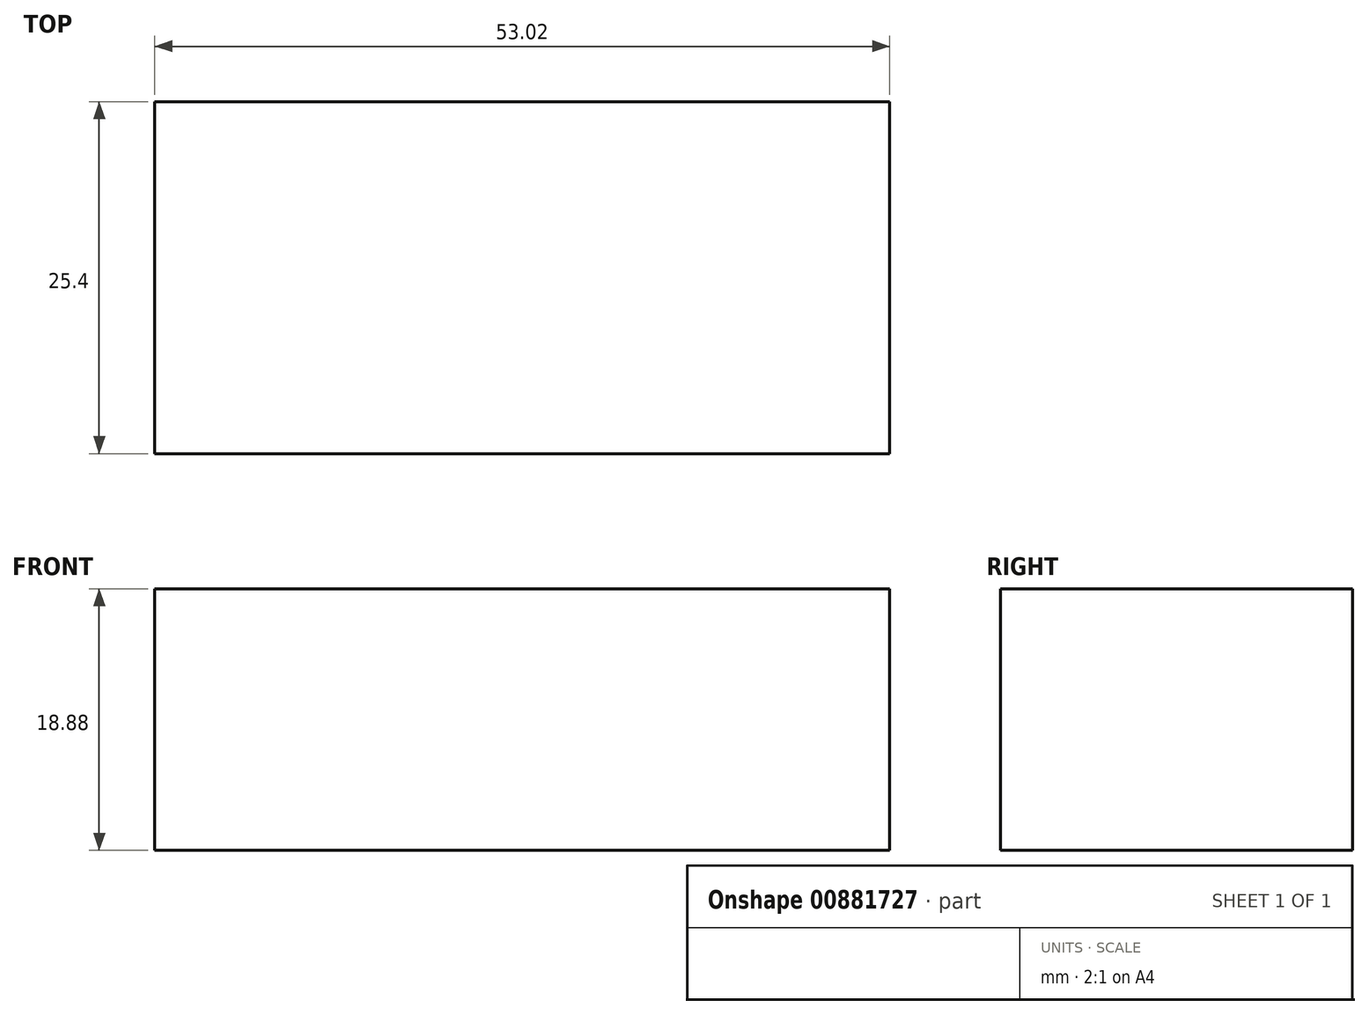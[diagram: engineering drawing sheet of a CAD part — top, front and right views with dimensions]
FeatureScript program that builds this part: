
annotation { "Feature Type Name" : "Feature", "Feature Type Description" : "" }
export const myFeature = defineFeature(function(context is Context, id is Id, definition is map)
    precondition{}
    {
        {
            var Q0;
            Q0=qCreatedBy(makeId("Front.planeOp"),FACE);
            var sketch = newSketch(context, id + "F0", { "sketchPlane" : qUnion([Q0])});
            skLineSegment(sketch, "E0.bottom", {"start": v(-113.42, 58.37) * mm, "end": v(-60.4, 58.37) * mm});
            skLineSegment(sketch, "E0.top", {"start": v(-113.42, 39.49) * mm, "end": v(-60.4, 39.49) * mm});
            skLineSegment(sketch, "E0.left", {"start": v(-113.42, 58.37) * mm, "end": v(-113.42, 39.49) * mm});
            skLineSegment(sketch, "E0.right", {"start": v(-60.4, 58.37) * mm, "end": v(-60.4, 39.49) * mm});
            skSolve(sketch);
        }
        {
            var Q0;
            Q0 = qSketchRegion(id + "F0", true);
            extrude(context, id + "F1", {"entities" : qUnion([Q0]), "depth" : 25.4 * mm, "offsetDistance" : 25.4 * mm});
        }
    });
